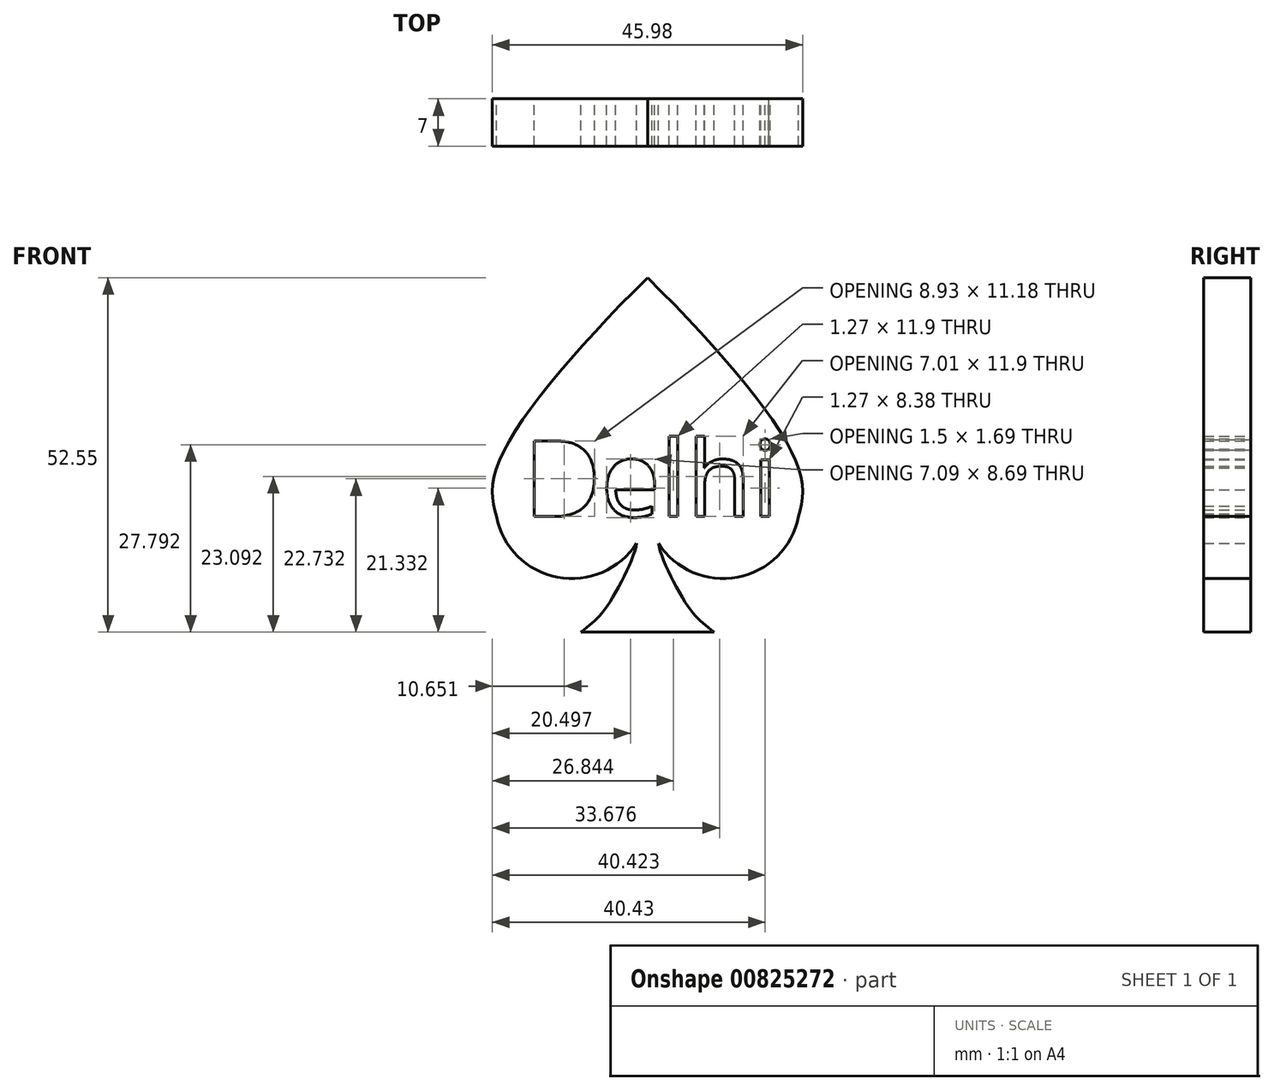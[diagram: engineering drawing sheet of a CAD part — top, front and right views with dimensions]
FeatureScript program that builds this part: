
annotation { "Feature Type Name" : "Feature", "Feature Type Description" : "" }
export const myFeature = defineFeature(function(context is Context, id is Id, definition is map)
    precondition{}
    {
        {
            var Q0;
            Q0=qCreatedBy(makeId("Front.planeOp"),FACE);
            var sketch = newSketch(context, id + "F0", { "sketchPlane" : qUnion([Q0])});
            skArc(sketch, "E0", {"start": v(-22.41, 0) * mm, "mid": v(-11.2, -9.2) * mm, "end": v(0, 0) * mm});
            skLineSegment(sketch, "E1.direction1", {"start": v(-22.41, 0) * mm, "end": v(2.99, 0) * mm, "construction": true});
            skFitSpline(sketch, "E2", {"points": [v(-22.41, 0) * mm, v(-22.41, 7.13) * mm, v(0, 35.41) * mm], "startDerivative": vector(-5.31, 20.82) * mm, "endDerivative": vector(47.06, 46.64) * mm});
            skArc(sketch, "E3.MirrorCS", {"start": v(22.41, 0) * mm, "mid": v(11.2, -9.2) * mm, "end": v(0, 0) * mm});
            skFitSpline(sketch, "E4.MirrorCS", {"points": [v(22.41, 0) * mm, v(22.41, 7.13) * mm, v(0, 35.41) * mm], "startDerivative": vector(5.31, 20.82) * mm, "endDerivative": vector(-47.06, 46.64) * mm});
            skFitSpline(sketch, "E5", {"points": [v(-1.6, -3.96) * mm, v(-6.26, -13.67) * mm, v(-9.88, -17.14) * mm], "startDerivative": vector(-1.92, -11.45) * mm, "endDerivative": vector(-10.8, -8.74) * mm});
            skFitSpline(sketch, "E6.MirrorCS", {"points": [v(1.6, -3.96) * mm, v(6.26, -13.67) * mm, v(9.88, -17.14) * mm], "startDerivative": vector(1.92, -11.45) * mm, "endDerivative": vector(10.8, -8.74) * mm});
            skLineSegment(sketch, "E7", {"start": v(-9.88, -17.14) * mm, "end": v(9.88, -17.14) * mm});
            skText(sketch, "E8", { "text": "Delhi", "fontName": "OpenSans-Regular.ttf"});
            const initialGuessF0  = {"E8": [-0.01834, 0, 1, 0, 0.01128]};
            skSetInitialGuess(sketch, initialGuessF0);
            skSolve(sketch);
        }
        {
            var Q0;
            Q0=makeQuery(id+"F0.imprint","IMPRINT",FACE,{"disambiguationData":[TD([[makeQuery(id+"F0.imprint","IMPRINT",EDGE,{"derivedFrom":sQuery(id+"F0.wireOp",EDGE,"E0")}),1.0]])]});
            var Q1;
            Q1=makeQuery(id+"F0.imprint","IMPRINT",FACE,{"disambiguationData":[TD([[makeQuery(id+"F0.imprint","IMPRINT",EDGE,{"derivedFrom":sQuery(id+"F0.wireOp",EDGE,"GEmRh5T7-9m1l-IO3P-cg7f-WZtUx2R7elqz")}),-1.0]])]});
            extrude(context, id + "F1", {"entities" : qUnion([Q0, Q1]), "depth" : 7 * mm, "offsetDistance" : 25 * mm});
        }
        {
            var Q0;
            {var subQ4=sQuery(id+"F0.wireOp",EDGE,"E5");Q0=makeQuery(id+"F0.imprint","IMPRINT",FACE,{"disambiguationData":[TD([[makeQuery(id+"F0.imprint","IMPRINT",EDGE,{"derivedFrom":subQ4}),1.0]])]});}
            extrude(context, id + "F2", {"entities" : qUnion([Q0]), "operationType" : NewBodyOperationType.ADD, "depth" : 7 * mm, "offsetDistance" : 25 * mm});
        }
    });
